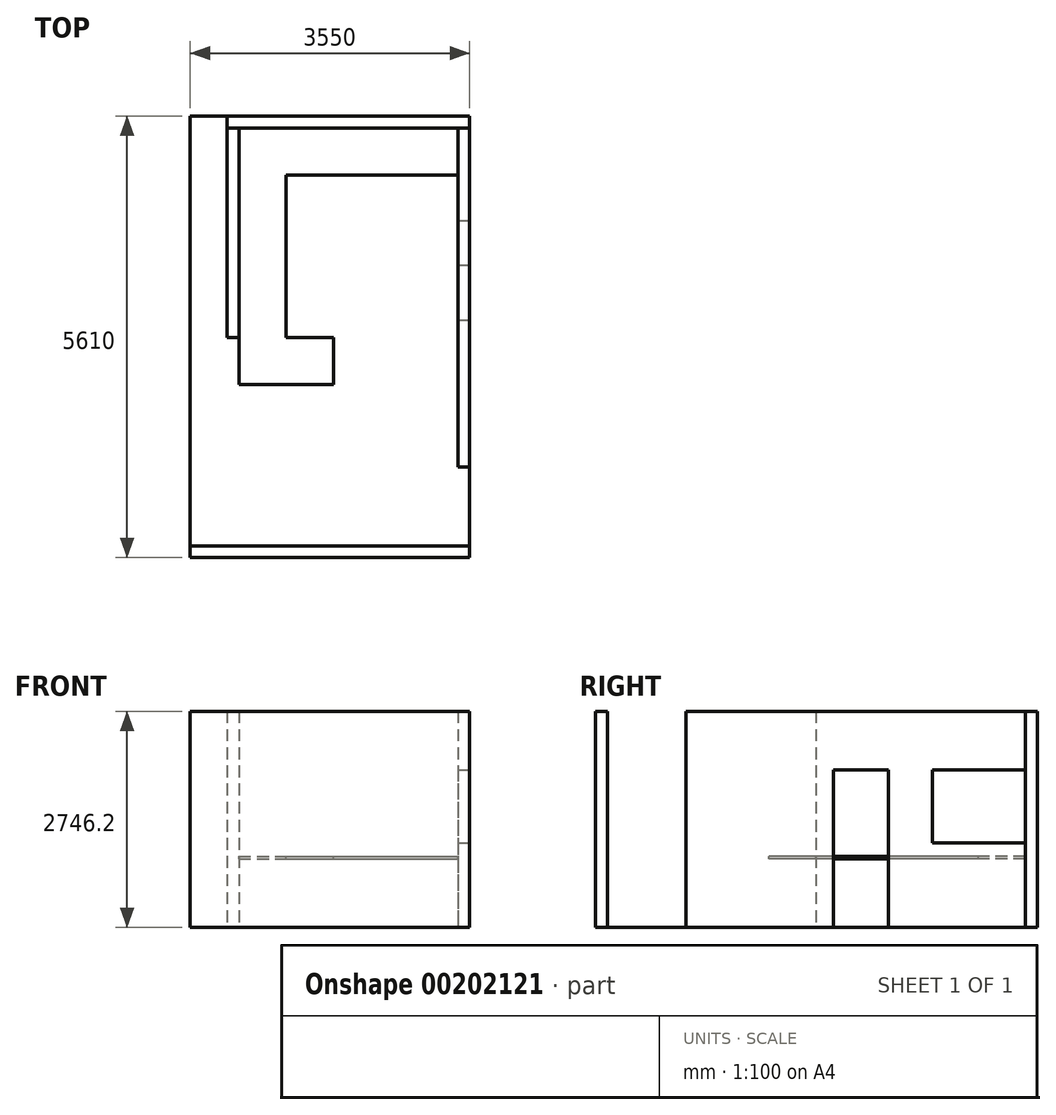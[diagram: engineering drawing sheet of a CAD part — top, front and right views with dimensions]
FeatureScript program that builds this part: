
annotation { "Feature Type Name" : "Feature", "Feature Type Description" : "" }
export const myFeature = defineFeature(function(context is Context, id is Id, definition is map)
    precondition{}
    {
        {
            var Q0;
            Q0=qCreatedBy(makeId("Top.planeOp"),FACE);
            cPlane(context, id + "F0", {"entities" : qUnion([Q0]), "cplaneType" : CPlaneType.OFFSET, "offset" : 1070 * mm, "width" : 150 * mm, "height" : 150 * mm});
        }
        {
            var Q0;
            Q0=qCreatedBy(makeId("Top.planeOp"),FACE);
            cPlane(context, id + "F1", {"entities" : qUnion([Q0]), "cplaneType" : CPlaneType.OFFSET, "offset" : 100 * mm, "width" : 150 * mm, "height" : 150 * mm});
        }
        {
            var Q0;
            Q0=qCreatedBy(makeId("Top.planeOp"),FACE);
            cPlane(context, id + "F2", {"entities" : qUnion([Q0]), "cplaneType" : CPlaneType.OFFSET, "offset" : 900 * mm, "width" : 150 * mm, "height" : 150 * mm});
        }
        {
            var Q0;
            Q0=qCreatedBy(makeId("Top.planeOp"),FACE);
            var sketch = newSketch(context, id + "F3", { "sketchPlane" : qUnion([Q0])});
            skLineSegment(sketch, "E0.bottom", {"start": v(0, 0) * mm, "end": v(3080, 0) * mm});
            skLineSegment(sketch, "E0.top", {"start": v(0, -150) * mm, "end": v(3080, -150) * mm});
            skLineSegment(sketch, "E0.left", {"start": v(0, 0) * mm, "end": v(0, -150) * mm});
            skLineSegment(sketch, "E0.right", {"start": v(3080, 0) * mm, "end": v(3080, -150) * mm});
            skSolve(sketch);
        }
        {
            var Q0;
            Q0=qSketchRegion(id+"F3",true);
            extrude(context, id + "F4", {"entities" : qUnion([Q0]), "depth" : 2743.2 * mm});
        }
        {
            var Q0;
            Q0=qCreatedBy(makeId("Top.planeOp"),FACE);
            var sketch = newSketch(context, id + "F5", { "sketchPlane" : qUnion([Q0])});
            skLineSegment(sketch, "E1.0", {"start": v(0, -150) * mm, "end": v(3080, -150) * mm});
            skLineSegment(sketch, "E2.bottom", {"start": v(0, -150) * mm, "end": v(150, -150) * mm});
            skLineSegment(sketch, "E2.top", {"start": v(0, -2810) * mm, "end": v(150, -2810) * mm});
            skLineSegment(sketch, "E2.left", {"start": v(0, -150) * mm, "end": v(0, -2810) * mm});
            skLineSegment(sketch, "E2.right", {"start": v(150, -150) * mm, "end": v(150, -2810) * mm});
            skSolve(sketch);
        }
        {
            var Q0;
            Q0=qSketchRegion(id+"F5",true);
            var Q1;
            Q1=makeQuery(id+"F4.opExtrude","CAP_FACE",FACE,{"disambiguationData":[OSD([sQuery(id+"F3.wireOp",EDGE,"E0.bottom"),sQuery(id+"F3.wireOp",EDGE,"E0.top"),sQuery(id+"F3.wireOp",EDGE,"E0.left"),sQuery(id+"F3.wireOp",EDGE,"E0.right")])],"isStart":false});
            extrude(context, id + "F6", {"entities" : qUnion([Q0]), "endBound" : BoundingType.UP_TO_SURFACE, "endBoundEntityFace" : qUnion([Q1]), "depth" : 2590 * mm});
        }
        {
            var Q0;
            Q0=qCreatedBy(makeId("Top.planeOp"),FACE);
            var sketch = newSketch(context, id + "F7", { "sketchPlane" : qUnion([Q0])});
            skLineSegment(sketch, "E3.0", {"start": v(0, -150) * mm, "end": v(3080, -150) * mm});
            skLineSegment(sketch, "E4.bottom", {"start": v(3080, -150) * mm, "end": v(2930, -150) * mm});
            skLineSegment(sketch, "E4.top", {"start": v(3080, -4460) * mm, "end": v(2930, -4460) * mm});
            skLineSegment(sketch, "E4.left", {"start": v(3080, -150) * mm, "end": v(3080, -4460) * mm});
            skLineSegment(sketch, "E4.right", {"start": v(2930, -150) * mm, "end": v(2930, -4460) * mm});
            skSolve(sketch);
        }
        {
            var Q0;
            Q0=qSketchRegion(id+"F7",true);
            var Q1;
            Q1=makeQuery(id+"F4.opExtrude","CAP_FACE",FACE,{"disambiguationData":[OSD([sQuery(id+"F3.wireOp",EDGE,"E0.bottom"),sQuery(id+"F3.wireOp",EDGE,"E0.top"),sQuery(id+"F3.wireOp",EDGE,"E0.left"),sQuery(id+"F3.wireOp",EDGE,"E0.right")])],"isStart":false});
            extrude(context, id + "F8", {"entities" : qUnion([Q0]), "endBound" : BoundingType.UP_TO_SURFACE, "endBoundEntityFace" : qUnion([Q1]), "depth" : 2590 * mm});
        }
        {
            var Q0;
            Q0=qCreatedBy(makeId("Top.planeOp"),FACE);
            var sketch = newSketch(context, id + "F9", { "sketchPlane" : qUnion([Q0])});
            skLineSegment(sketch, "E5.bottom", {"start": v(3080, -5610) * mm, "end": v(-470, -5610) * mm});
            skLineSegment(sketch, "E5.top", {"start": v(3080, -5460) * mm, "end": v(-470, -5460) * mm});
            skLineSegment(sketch, "E5.left", {"start": v(3080, -5610) * mm, "end": v(3080, -5460) * mm});
            skLineSegment(sketch, "E5.right", {"start": v(-470, -5610) * mm, "end": v(-470, -5460) * mm});
            skSolve(sketch);
        }
        {
            var Q0;
            Q0=qSketchRegion(id+"F9",true);
            var Q1;
            Q1=makeQuery(id+"F4.opExtrude","CAP_FACE",FACE,{"disambiguationData":[OSD([sQuery(id+"F3.wireOp",EDGE,"E0.bottom"),sQuery(id+"F3.wireOp",EDGE,"E0.top"),sQuery(id+"F3.wireOp",EDGE,"E0.left"),sQuery(id+"F3.wireOp",EDGE,"E0.right")])],"isStart":false});
            extrude(context, id + "F10", {"entities" : qUnion([Q0]), "endBound" : BoundingType.UP_TO_SURFACE, "endBoundEntityFace" : qUnion([Q1]), "depth" : 2590 * mm});
        }
        {
            var Q0;
            Q0=qCreatedBy(makeId("Top.planeOp"),FACE);
            var sketch = newSketch(context, id + "F11", { "sketchPlane" : qUnion([Q0])});
            skLineSegment(sketch, "E6.bottom", {"start": v(-470, 0) * mm, "end": v(3080, 0) * mm});
            skLineSegment(sketch, "E6.top", {"start": v(-470, -5610) * mm, "end": v(3080, -5610) * mm});
            skLineSegment(sketch, "E6.left", {"start": v(-470, 0) * mm, "end": v(-470, -5610) * mm});
            skLineSegment(sketch, "E6.right", {"start": v(3080, 0) * mm, "end": v(3080, -5610) * mm});
            skSolve(sketch);
        }
        {
            var Q0;
            Q0=qSketchRegion(id+"F11",true);
            extrude(context, id + "F12", {"entities" : qUnion([Q0]), "oppositeDirection" : true, "depth" : 3 * mm});
        }
        {
            var Q0;
            Q0=qCreatedBy(makeId("Top.planeOp"),FACE);
            var sketch = newSketch(context, id + "F13", { "sketchPlane" : qUnion([Q0])});
            skLineSegment(sketch, "E7.bottom", {"start": v(2930, -1890) * mm, "end": v(3080, -1890) * mm});
            skLineSegment(sketch, "E7.top", {"start": v(2930, -2590) * mm, "end": v(3080, -2590) * mm});
            skLineSegment(sketch, "E7.left", {"start": v(2930, -1890) * mm, "end": v(2930, -2590) * mm});
            skLineSegment(sketch, "E7.right", {"start": v(3080, -1890) * mm, "end": v(3080, -2590) * mm});
            skSolve(sketch);
        }
        {
            var Q0;
            Q0=qSketchRegion(id+"F13",true);
            extrude(context, id + "F14", {"entities" : qUnion([Q0]), "operationType" : NewBodyOperationType.REMOVE, "depth" : 2000 * mm});
        }
        {
            var Q0;
            Q0=qCreatedBy(id+"F0.planeOp",FACE);
            var sketch = newSketch(context, id + "F15", { "sketchPlane" : qUnion([Q0])});
            skLineSegment(sketch, "E8.bottom", {"start": v(2930, -150) * mm, "end": v(3080, -150) * mm});
            skLineSegment(sketch, "E8.top", {"start": v(2930, -1330) * mm, "end": v(3080, -1330) * mm});
            skLineSegment(sketch, "E8.left", {"start": v(2930, -150) * mm, "end": v(2930, -1330) * mm});
            skLineSegment(sketch, "E8.right", {"start": v(3080, -150) * mm, "end": v(3080, -1330) * mm});
            skSolve(sketch);
        }
        {
            var Q0;
            Q0=qSketchRegion(id+"F15",true);
            var Q1;
            Q1=makeQuery(id+"F14.boolean.opBoolean","COPY",FACE,{"derivedFrom":makeQuery(id+"F14.opExtrude","CAP_FACE",FACE,{"disambiguationData":[OSD([sQuery(id+"F13.wireOp",EDGE,"E7.bottom"),sQuery(id+"F13.wireOp",EDGE,"E7.top"),sQuery(id+"F13.wireOp",EDGE,"E7.left"),sQuery(id+"F13.wireOp",EDGE,"E7.right")])],"isStart":false})});
            extrude(context, id + "F16", {"entities" : qUnion([Q0]), "operationType" : NewBodyOperationType.REMOVE, "endBound" : BoundingType.UP_TO_SURFACE, "endBoundEntityFace" : qUnion([Q1]), "depth" : 25 * mm});
        }
        {
            var Q0;
            Q0=qCreatedBy(id+"F2.planeOp",FACE);
            var sketch = newSketch(context, id + "F17", { "sketchPlane" : qUnion([Q0])});
            skLineSegment(sketch, "E9.bottom", {"start": v(150, -150) * mm, "end": v(2930, -150) * mm});
            skLineSegment(sketch, "E9.top", {"start": v(150, -750) * mm, "end": v(2930, -750) * mm});
            skLineSegment(sketch, "E9.left", {"start": v(150, -150) * mm, "end": v(150, -750) * mm});
            skLineSegment(sketch, "E9.right", {"start": v(2930, -150) * mm, "end": v(2930, -750) * mm});
            skLineSegment(sketch, "E10.bottom", {"start": v(150, -750) * mm, "end": v(750, -750) * mm});
            skLineSegment(sketch, "E10.top", {"start": v(150, -2810) * mm, "end": v(750, -2810) * mm});
            skLineSegment(sketch, "E10.left", {"start": v(150, -750) * mm, "end": v(150, -2810) * mm});
            skLineSegment(sketch, "E10.right", {"start": v(750, -750) * mm, "end": v(750, -2810) * mm});
            skLineSegment(sketch, "E11.bottom", {"start": v(150, -2810) * mm, "end": v(1350, -2810) * mm});
            skLineSegment(sketch, "E11.top", {"start": v(150, -3410) * mm, "end": v(1350, -3410) * mm});
            skLineSegment(sketch, "E11.left", {"start": v(150, -2810) * mm, "end": v(150, -3410) * mm});
            skLineSegment(sketch, "E11.right", {"start": v(1350, -2810) * mm, "end": v(1350, -3410) * mm});
            skSolve(sketch);
        }
        {
            var Q0;
            Q0 = qSketchRegion(id + "F17", true);
            extrude(context, id + "F18", {"entities" : qUnion([Q0]), "oppositeDirection" : true, "depth" : 30 * mm});
        }
    });
